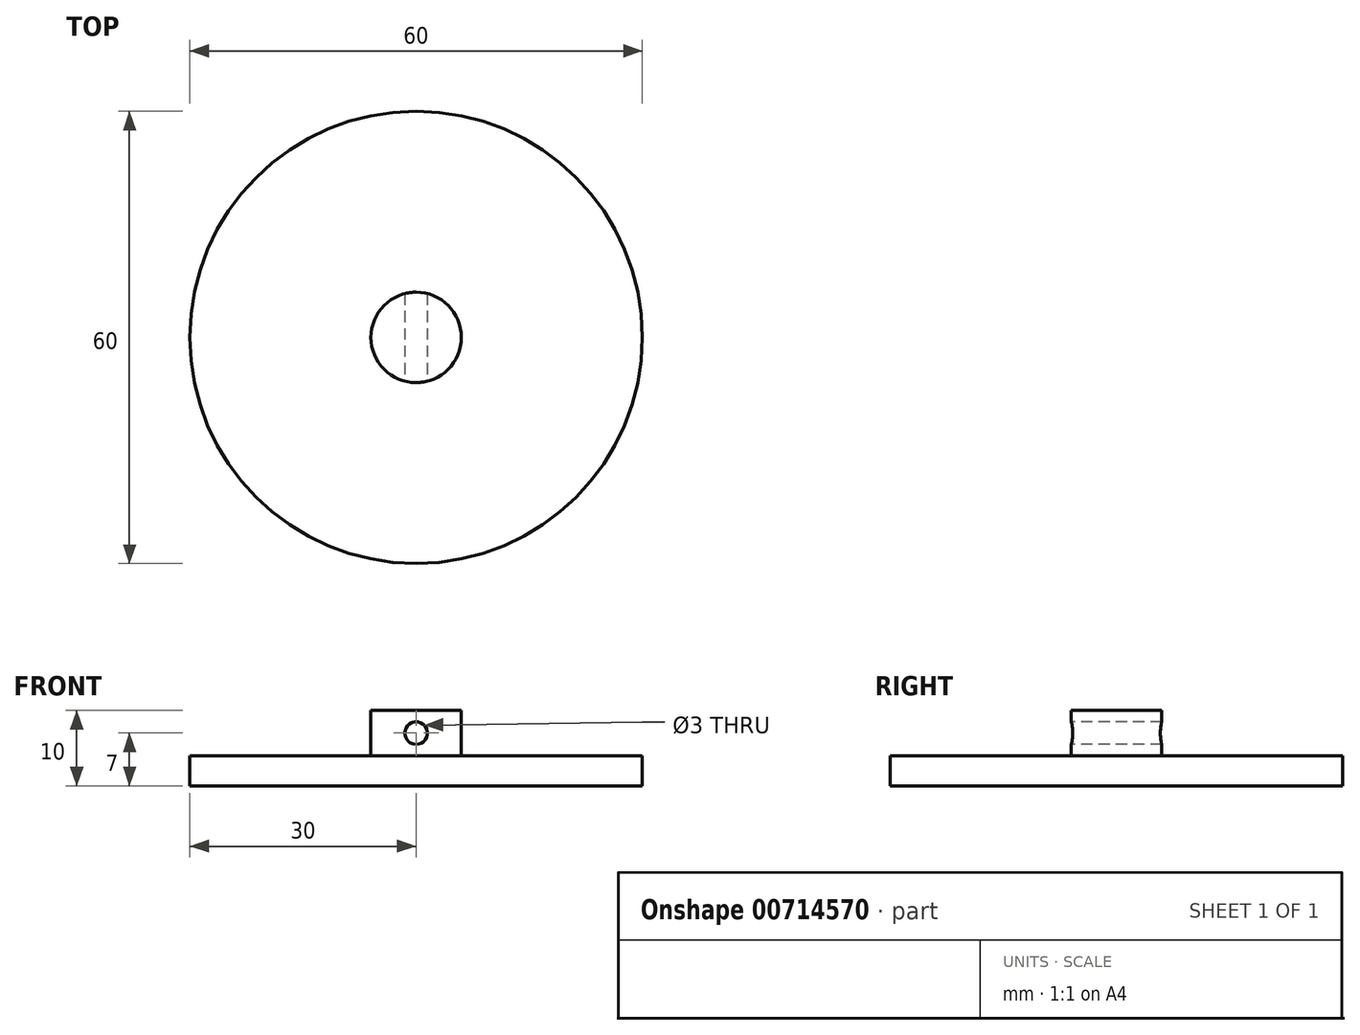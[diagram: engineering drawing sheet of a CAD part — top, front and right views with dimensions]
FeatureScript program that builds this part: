
annotation { "Feature Type Name" : "Feature", "Feature Type Description" : "" }
export const myFeature = defineFeature(function(context is Context, id is Id, definition is map)
    precondition{}
    {
        {
            var Q0;
            Q0=qCreatedBy(makeId("Top.planeOp"),FACE);
            var sketch = newSketch(context, id + "F0", { "sketchPlane" : qUnion([Q0])});
            skCircle(sketch, "E0", {"center": v(0, 0) * mm, "radius": 30 * mm});
            skCircle(sketch, "E1", {"center": v(0, 0) * mm, "radius": 6 * mm});
            skSolve(sketch);
        }
        {
            var Q0;
            Q0=makeQuery(id+"F0.imprint","IMPRINT",FACE,{"disambiguationData":[TD([[makeQuery(id+"F0.imprint","IMPRINT",EDGE,{"derivedFrom":sQuery(id+"F0.wireOp",EDGE,"E0")}),1.0]])]});
            var Q1;
            Q1=makeQuery(id+"F0.imprint","IMPRINT",FACE,{"disambiguationData":[TD([[makeQuery(id+"F0.imprint","IMPRINT",EDGE,{"derivedFrom":sQuery(id+"F0.wireOp",EDGE,"E1")}),1.0]])]});
            extrude(context, id + "F1", {"entities" : qUnion([Q0, Q1]), "oppositeDirection" : true, "depth" : 4 * mm, "offsetDistance" : 25 * mm});
        }
        {
            var Q0;
            Q0=makeQuery(id+"F0.imprint","IMPRINT",FACE,{"disambiguationData":[TD([[makeQuery(id+"F0.imprint","IMPRINT",EDGE,{"derivedFrom":sQuery(id+"F0.wireOp",EDGE,"E1")}),1.0]])]});
            extrude(context, id + "F2", {"entities" : qUnion([Q0]), "operationType" : NewBodyOperationType.ADD, "depth" : 6 * mm, "offsetDistance" : 25 * mm});
        }
        {
            var Q0;
            Q0=qCreatedBy(makeId("Front.planeOp"),FACE);
            var sketch = newSketch(context, id + "F3", { "sketchPlane" : qUnion([Q0])});
            skCircle(sketch, "E2", {"center": v(0, 3) * mm, "radius": 1.5 * mm});
            skSolve(sketch);
        }
        {
            var Q0;
            Q0 = qSketchRegion(id + "F3", true);
            extrude(context, id + "F4", {"entities" : qUnion([Q0]), "operationType" : NewBodyOperationType.REMOVE, "endBound" : BoundingType.SYMMETRIC, "oppositeDirection" : true, "depth" : 25 * mm, "offsetDistance" : 25 * mm});
        }
    });
